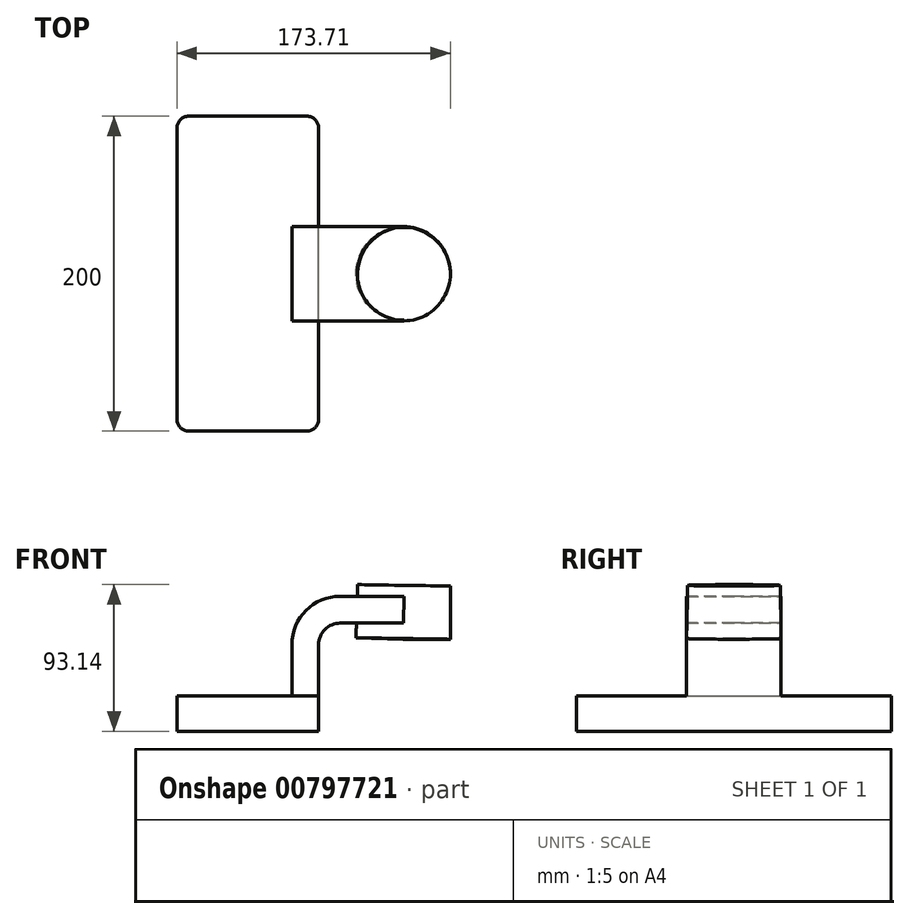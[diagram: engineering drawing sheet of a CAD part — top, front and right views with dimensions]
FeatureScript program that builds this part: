
annotation { "Feature Type Name" : "Feature", "Feature Type Description" : "" }
export const myFeature = defineFeature(function(context is Context, id is Id, definition is map)
    precondition{}
    {
        {
            var Q0;
            Q0=qCreatedBy(makeId("Front.planeOp"),FACE);
            var sketch = newSketch(context, id + "F0", { "sketchPlane" : qUnion([Q0])});
            skLineSegment(sketch, "E0.bottom", {"start": v(-45, -11.25) * mm, "end": v(45, -11.25) * mm});
            skLineSegment(sketch, "E0.top", {"start": v(-45, 11.25) * mm, "end": v(45, 11.25) * mm});
            skLineSegment(sketch, "E0.left", {"start": v(-45, -11.25) * mm, "end": v(-45, 11.25) * mm});
            skLineSegment(sketch, "E0.right", {"start": v(45, -11.25) * mm, "end": v(45, 11.25) * mm});
            skPoint(sketch, "E0.middle", {"position": v(0, 0) * mm});
            skLineSegment(sketch, "E1.bottom", {"start": v(68.7, 47.2) * mm, "end": v(128.7, 47.2) * mm});
            skLineSegment(sketch, "E1.top", {"start": v(68.7, 80.96) * mm, "end": v(128.7, 80.96) * mm});
            skLineSegment(sketch, "E1.left", {"start": v(68.7, 47.2) * mm, "end": v(68.7, 80.96) * mm});
            skLineSegment(sketch, "E1.right", {"start": v(128.7, 47.2) * mm, "end": v(128.7, 80.96) * mm});
            skPoint(sketch, "E1.middle", {"position": v(98.7, 64.08) * mm});
            skLineSegment(sketch, "E2", {"start": v(45, 11.25) * mm, "end": v(45, 43.75) * mm});
            skArc(sketch, "E3", {"start": v(45, 43.75) * mm, "mid": v(49.02, 53.44) * mm, "end": v(58.7, 57.46) * mm});
            skLineSegment(sketch, "E4", {"start": v(58.7, 57.46) * mm, "end": v(99.24, 57.46) * mm});
            skLineSegment(sketch, "E5.0", {"start": v(58.7, 74.46) * mm, "end": v(99.24, 74.46) * mm});
            skArc(sketch, "E5.1", {"start": v(28, 43.75) * mm, "mid": v(37, 65.46) * mm, "end": v(58.7, 74.46) * mm});
            skLineSegment(sketch, "E5.2", {"start": v(28, 11.25) * mm, "end": v(28, 43.75) * mm});
            skLineSegment(sketch, "E6", {"start": v(98.7, 47.2) * mm, "end": v(99.24, 80.96) * mm});
            skFitSpline(sketch, "E7", {"points": [v(-45, 11.25) * mm, v(58.7, 74.46) * mm], "startDerivative": vector(16.56, 134.6) * mm, "endDerivative": vector(121.57, -0.85) * mm});
            skSolve(sketch);
        }
        {
            var Q0;
            Q0=makeQuery(id+"F0.imprint","IMPRINT",FACE,{"disambiguationData":[TD([[makeQuery(id+"F0.imprint","IMPRINT",EDGE,{"derivedFrom":sQuery(id+"F0.wireOp",EDGE,"E0.bottom")}),1.0]])]});
            extrude(context, id + "F1", {"entities" : qUnion([Q0]), "endBound" : BoundingType.SYMMETRIC, "depth" : 200 * mm, "offsetDistance" : 25 * mm});
        }
        {
            var Q0;
            {var subQ1=sQuery(id+"F0.wireOp",EDGE,"E2");Q0=makeQuery(id+"F0.imprint","IMPRINT",FACE,{"disambiguationData":[TD([[makeQuery(id+"F0.imprint","IMPRINT",EDGE,{"derivedFrom":subQ1}),1.0]])]});}
            var Q1;
            {var subQ0=sQuery(id+"F0.wireOp",EDGE,"E4");var subQ1=sQuery(id+"F0.wireOp",EDGE,"E1.left");var subQ2=makeQuery(id+"F0.imprint","INTERSECT",VERTEX,{"derivedFrom":[subQ1,subQ0]});Q1=makeQuery(id+"F0.imprint","IMPRINT",FACE,{"disambiguationData":[TD([[makeQuery(id+"F0.imprint","IMPRINT",EDGE,{"disambiguationData":[TD([[subQ2,-1.0]])],"derivedFrom":subQ1}),-1.0]])]});}
            extrude(context, id + "F2", {"entities" : qUnion([Q0, Q1]), "operationType" : NewBodyOperationType.ADD, "endBound" : BoundingType.SYMMETRIC, "depth" : 60 * mm, "offsetDistance" : 25 * mm});
        }
        {
            var Q0;
            Q0=makeQuery(id+"F0.imprint","IMPRINT",FACE,{"disambiguationData":[TD([[makeQuery(id+"F0.imprint","IMPRINT",EDGE,{"derivedFrom":sQuery(id+"F0.wireOp",EDGE,"E5.1")}),1.0]])]});
            extrude(context, id + "F3", {"entities" : qUnion([Q0]), "operationType" : NewBodyOperationType.ADD, "endBound" : BoundingType.SYMMETRIC, "depth" : 8 * mm, "offsetDistance" : 25 * mm});
        }
        {
            var Q0;
            {var subQ0=sQuery(id+"F0.wireOp",EDGE,"E1.right");Q0=makeQuery(id+"F0.imprint","IMPRINT",FACE,{"disambiguationData":[TD([[makeQuery(id+"F0.imprint","IMPRINT",EDGE,{"derivedFrom":subQ0}),1.0]])]});}
            var Q1;
            Q1=sQuery(id+"F0.wireOp",EDGE,"E6");
            revolve(context, id + "F4", {"operationType" : NewBodyOperationType.ADD, "surfaceOperationType" : NewSurfaceOperationType.NEW, "entities" : qUnion([Q0]), "axis" : qUnion([Q1]), "revolveType" : RevolveType.FULL});
        }
        {
            var Q0;
            Q0=makeQuery(id+"F1.opExtrude","CAP_EDGE",EDGE,{"disambiguationData":[OSD([sQuery(id+"F0.wireOp",EDGE,"E0.left")])],"isStart":false});
            var Q1;
            Q1=makeQuery(id+"F1.opExtrude","CAP_EDGE",EDGE,{"disambiguationData":[OSD([sQuery(id+"F0.wireOp",EDGE,"E0.left")])],"isStart":true});
            var Q2;
            Q2=makeQuery(id+"F1.opExtrude","CAP_EDGE",EDGE,{"disambiguationData":[OSD([sQuery(id+"F0.wireOp",EDGE,"E0.right")])],"isStart":false});
            var Q3;
            Q3=makeQuery(id+"F1.opExtrude","CAP_EDGE",EDGE,{"disambiguationData":[OSD([sQuery(id+"F0.wireOp",EDGE,"E0.right")])],"isStart":true});
            fillet(context, id + "F5", {"entities" : qUnion([Q0, Q1, Q2, Q3]), "radius" : 7.5 * mm, "tangentPropagation" : true, "allowEdgeOverflow" : false});
        }
    });
